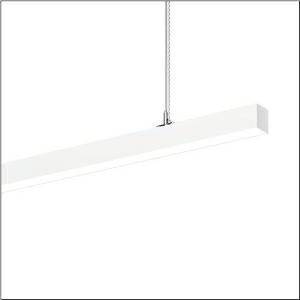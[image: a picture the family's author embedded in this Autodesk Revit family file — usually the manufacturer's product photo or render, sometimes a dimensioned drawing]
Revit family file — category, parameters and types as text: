
# Revit family: silica_21_51mx30da44wb
name_source: partatom
category: Lighting Fixtures
units: mm (PartAtom-declared; Revit-internal decimal feet)

## family parameters
Cut with Voids When Loaded = No
Host = Face
Light Source = No
Part Type = Normal
Room Calculation Point = No
Round Connector Dimension = Use Diameter
Shared = No

## types (1)
- --- (1 x LED, 4210 lm, 26 W, 4000K)
    Apparent Load = 26 VA
    CIE Flux Codes = 47 79 96 57 100
    Color Rendering = 80
    Color Temperature = 4000K
    Default Elevation = 1800 mm
    Description = Silica 21, office luminaire, primary optical cover: cover, of PMMA, opal, light emission: direct/indirect distribution, primary light characteristic: symmetric, installation type: suspended mounting, LED, rated luminous flux: 4.210lm, luminous efficacy: 162lm/W, light colour: 840, colour temperature: 4000K, control gear: DALI 2, with terminal, 3+2-pole, max. 2.5mm², mains connection: 220..240V, AC, 50/60Hz, rated input power: 26W, luminaire housing, of aluminium, traffic white (RAL 9016), length: 1.204mm, width: 53mm, height: 53mm, protection rating (complete): IP20, insulation class (complete): insulation class I (protective earthing), certification: CE, permissible operating ambient temperature: 0..+35°C, standard: EN 50419, packaging unit: 1 piece
    Height = 53 mm
    Lamp = 1 x LED
    Lamp Light Flux = 4210 lm
    Lamp Power = 26 W
    Lamp count = 1
    Length = 1204 mm
    Luminous efficacy = 162 lm/W
    Manufacturer = Siteco
    ModVariant = No
    Model = 51MX30DA44WB
    Mounting Place = Ceiling
    Mounting Type = Pendant
    Number of Poles = 1
    OnlyDefault = Yes
    Power Factor = 1
    Product Name = Silica 21
    Product group = office luminaire | ceiling pendant
    ProductGroupID = 903
    Protection Class = Protection class I
    Protection Degree = IP 20
    RLX_Detail_Level = 1
    RLX_Emergency_Light_Flux = 0 lm
    RLX_Emergency_Type = 0
    RLX_Emergency_Type_DB = No
    RlxData = <blob elided: 20609 chars, md5=f78717d8>
    Socket = socket
    Standby Power = 0 W
    System Light Flux = 4210 lm
    System Power = 26 W
    Type Comments = factory setting: luminous flux: 100 % | dim-lin: 254 | 218 mA
    Type Image = l_1349023.jpg
    URL = http://relux.com
    VarID = @adj_117681
    Voltage = 0 V
    Weight = 0.00 kg
    Width = 53 mm

## geometry (parser evidence)
native form markers: Blend x4, Sweep x11
no freeform markers — native parametric forms only
